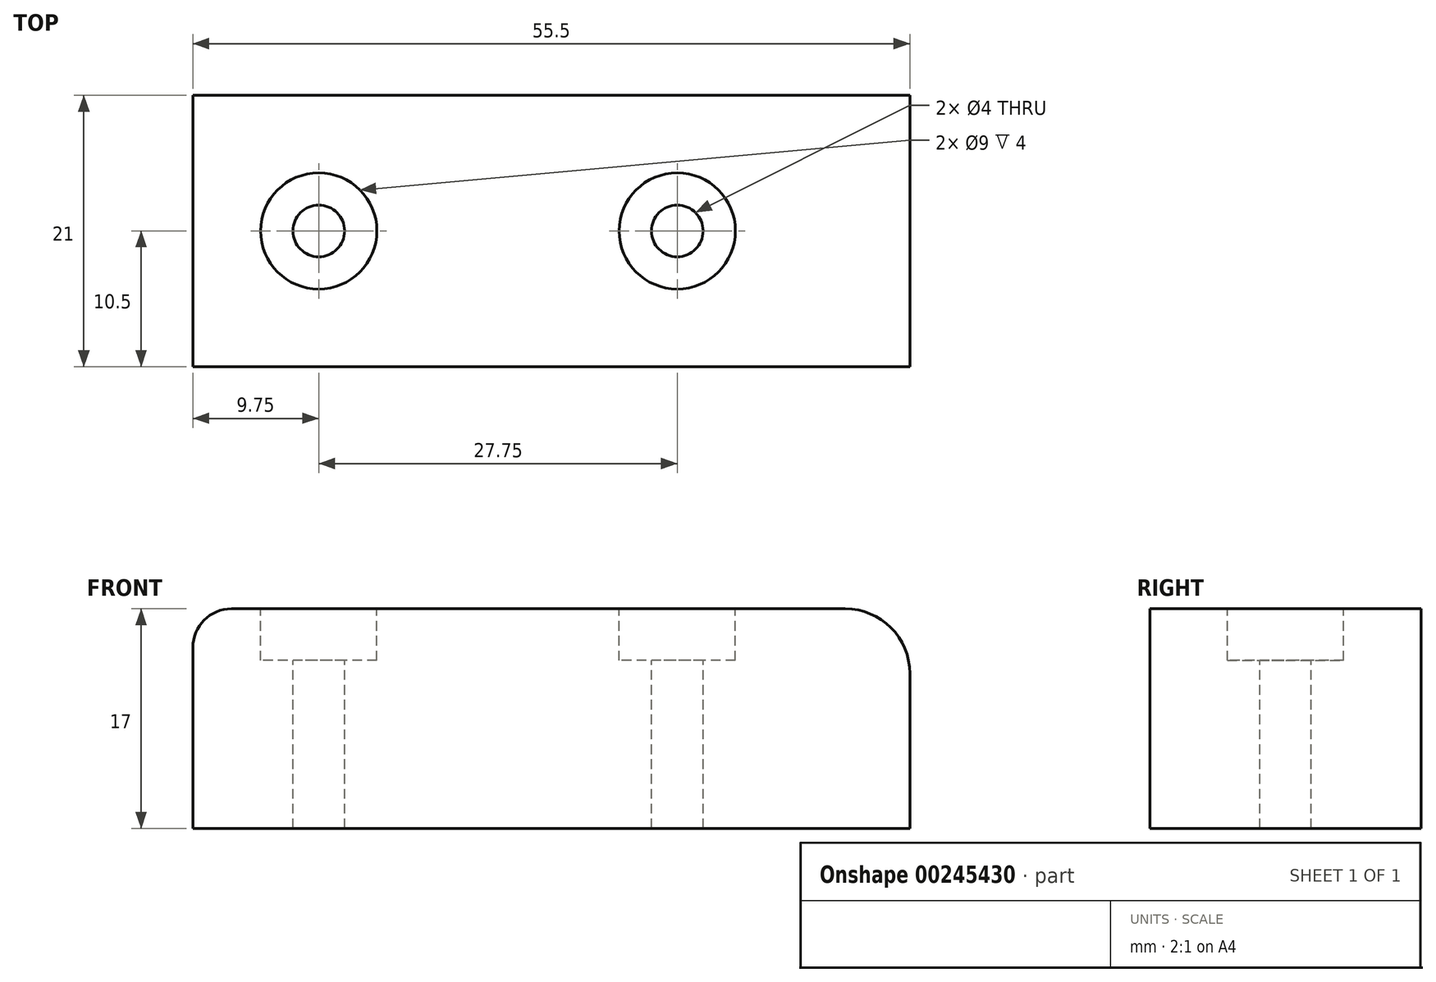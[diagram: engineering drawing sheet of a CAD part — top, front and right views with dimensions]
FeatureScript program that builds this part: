
annotation { "Feature Type Name" : "Feature", "Feature Type Description" : "" }
export const myFeature = defineFeature(function(context is Context, id is Id, definition is map)
    precondition{}
    {
        {
            var Q0;
            Q0=qCreatedBy(makeId("Front.planeOp"),FACE);
            var sketch = newSketch(context, id + "F0", { "sketchPlane" : qUnion([Q0])});
            skLineSegment(sketch, "E0.top", {"start": v(6.9, 17) * mm, "end": v(55.5, 17) * mm});
            skLineSegment(sketch, "E0.right", {"start": v(55.5, 0) * mm, "end": v(55.5, 17) * mm});
            skLineSegment(sketch, "E1", {"start": v(6.9, 17) * mm, "end": v(0, 17) * mm});
            skLineSegment(sketch, "E2", {"start": v(0, 17) * mm, "end": v(0, 0) * mm});
            skLineSegment(sketch, "E3", {"start": v(0, 0) * mm, "end": v(55.5, 0) * mm});
            skSolve(sketch);
        }
        {
            var Q0;
            Q0=qSketchRegion(id+"F0",true);
            extrude(context, id + "F1", {"entities" : qUnion([Q0]), "depth" : 21 * mm});
        }
        {
            var Q0;
            Q0=makeQuery(id+"F1.opExtrude","SWEPT_EDGE",EDGE,{"disambiguationData":[OSD([sQuery(id+"F0.wireOp",EDGE,"E0.top"),sQuery(id+"F0.wireOp",EDGE,"E0.right")])]});
            fillet(context, id + "F2", {"entities" : qUnion([Q0]), "radius" : 5 * mm, "tangentPropagation" : true, "allowEdgeOverflow" : false});
        }
        {
            var Q0;
            Q0=makeQuery(id+"F1.opExtrude","SWEPT_FACE",FACE,{"disambiguationData":[OSD([sQuery(id+"F0.wireOp",EDGE,"E0.top"),sQuery(id+"F0.wireOp",EDGE,"E1")])]});
            var sketch = newSketch(context, id + "F3", { "sketchPlane" : qUnion([Q0])});
            skLineSegment(sketch, "E4", {"start": v(0, -10.5) * mm, "end": v(19.5, -10.5) * mm});
            skLineSegment(sketch, "E5", {"start": v(19.5, -10.5) * mm, "end": v(55.5, -10.5) * mm});
            skCircle(sketch, "E6", {"center": v(9.75, -10.5) * mm, "radius": 2 * mm});
            skCircle(sketch, "E7", {"center": v(37.5, -10.5) * mm, "radius": 2 * mm});
            skSolve(sketch);
        }
        {
            var Q0;
            Q0=qSketchRegion(id+"F3",true);
            extrude(context, id + "F4", {"entities" : qUnion([Q0]), "operationType" : NewBodyOperationType.REMOVE, "oppositeDirection" : true, "depth" : 25 * mm});
        }
        {
            var Q0;
            Q0=makeQuery(id+"F1.opExtrude","SWEPT_EDGE",EDGE,{"disambiguationData":[OSD([sQuery(id+"F0.wireOp",EDGE,"E1"),sQuery(id+"F0.wireOp",EDGE,"E2")])]});
            fillet(context, id + "F5", {"entities" : qUnion([Q0]), "radius" : 3 * mm, "tangentPropagation" : true, "allowEdgeOverflow" : false});
        }
        {
            var Q0;
            Q0=makeQuery(id+"F1.opExtrude","SWEPT_FACE",FACE,{"disambiguationData":[OSD([sQuery(id+"F0.wireOp",EDGE,"E0.top"),sQuery(id+"F0.wireOp",EDGE,"E1")])]});
            var sketch = newSketch(context, id + "F6", { "sketchPlane" : qUnion([Q0])});
            skCircle(sketch, "E8", {"center": v(9.75, -10.5) * mm, "radius": 4.5 * mm});
            skCircle(sketch, "E9", {"center": v(37.5, -10.5) * mm, "radius": 4.5 * mm});
            skSolve(sketch);
        }
        {
            var Q0;
            Q0=qSketchRegion(id+"F6",true);
            extrude(context, id + "F7", {"entities" : qUnion([Q0]), "operationType" : NewBodyOperationType.REMOVE, "oppositeDirection" : true, "depth" : 4 * mm});
        }
    });
